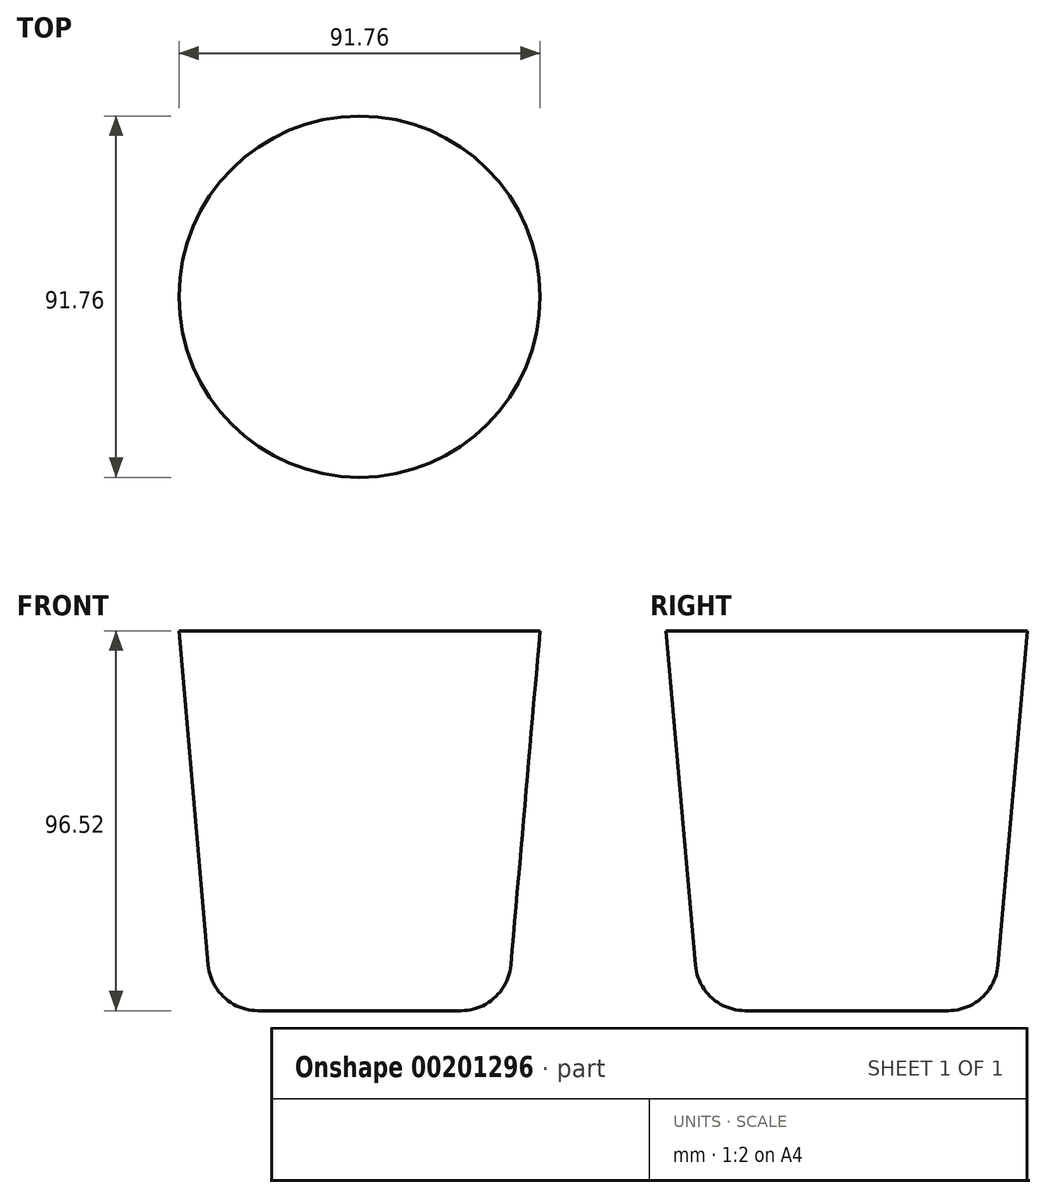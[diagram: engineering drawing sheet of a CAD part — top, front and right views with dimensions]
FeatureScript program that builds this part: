
annotation { "Feature Type Name" : "Feature", "Feature Type Description" : "" }
export const myFeature = defineFeature(function(context is Context, id is Id, definition is map)
    precondition{}
    {
        {
            var Q0;
            Q0=qCreatedBy(makeId("Top.planeOp"),FACE);
            var sketch = newSketch(context, id + "F0", { "sketchPlane" : qUnion([Q0])});
            skCircle(sketch, "E0", {"center": v(0, 0) * mm, "radius": 38.1 * mm});
            skSolve(sketch);
        }
        {
            var Q0;
            Q0 = qSketchRegion(id + "F0", true);
            extrude(context, id + "F1", {"entities" : qUnion([Q0]), "depth" : 88.9 * mm, "hasDraft" : true, "draftAngle" : 5 * degree, "hasSecondDirection" : true, "secondDirectionOppositeDirection" : true, "secondDirectionDepth" : 7.62 * mm});
        }
        {
            var Q0;
            Q0=makeQuery(id+"F1.opExtrude","CAP_EDGE",EDGE,{"disambiguationData":[OSD([sQuery(id+"F0.wireOp",EDGE,"E0")])],"isStart":true});
            fillet(context, id + "F2", {"entities" : qUnion([Q0]), "radius" : 12.7 * mm, "tangentPropagation" : true, "allowEdgeOverflow" : false});
        }
    });
